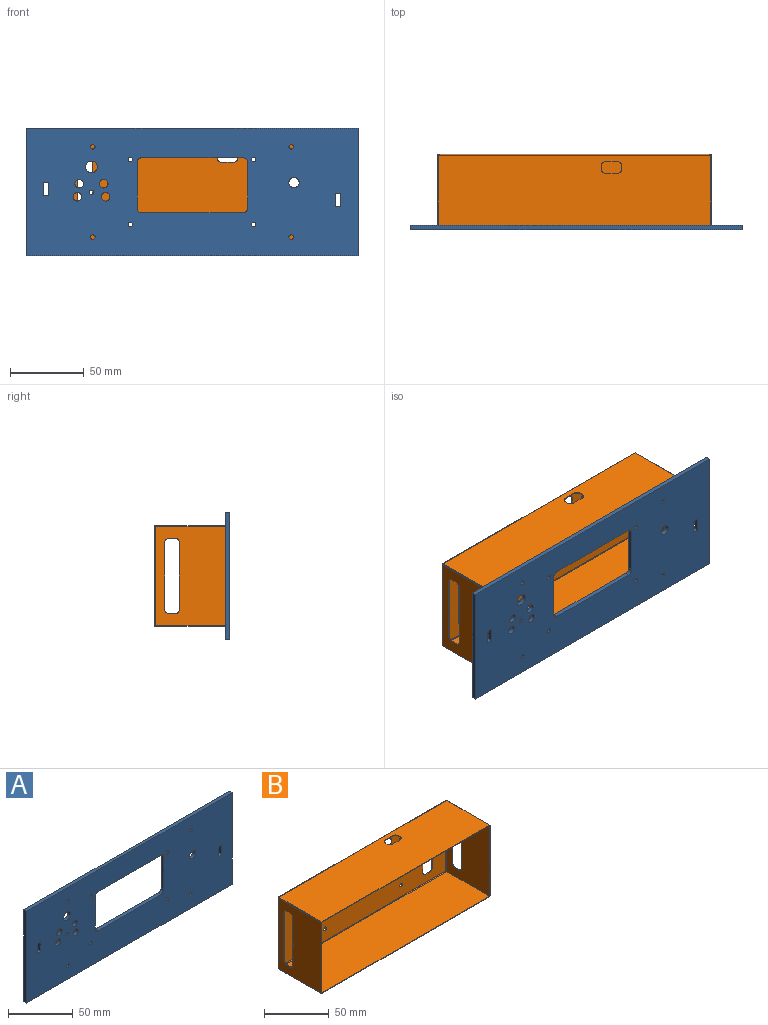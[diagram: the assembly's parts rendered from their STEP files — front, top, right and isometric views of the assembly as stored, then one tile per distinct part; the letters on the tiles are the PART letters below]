
ASSEMBLY  parts=2 mates=3
PART A: 37 faces, bbox 224.5x3x86.5 mm
  f0: plane 224.5x3mm, normal (0,0,1), area 673.5mm2, adj f1,f34,f35,f36
  f1: plane 86.5x3mm, normal (-1,0,0), area 259.5mm2, adj f0,f2,f35,f36
  f2: plane 224.5x3mm, normal (0,0,-1), area 673.5mm2, adj f1,f34,f35,f36
  f3: plane 9x3mm, normal (-1,0,0), area 27mm2, adj f4,f16,f35,f36
  f4: plane 4x3mm, normal (0,0,1), area 12mm2, adj f3,f5,f35,f36
  f5: plane 9x3mm, normal (1,0,0), area 27mm2, adj f4,f16,f35,f36
  f6: plane 9x3mm, normal (-1,0,0), area 27mm2, adj f7,f17,f35,f36
  f7: plane 4x3mm, normal (0,0,1), area 12mm2, adj f6,f8,f35,f36
  f8: plane 9x3mm, normal (1,0,0), area 27mm2, adj f7,f17,f35,f36
  f9: cylinder r=3mm len=3mm, axis (0,1,0), area 14.1mm2, adj f10,f18,f35,f36
  f10: plane 31x3mm, normal (-1,0,0), area 93mm2, adj f9,f11,f35,f36
  f11: cylinder r=3mm len=3mm, axis (0,1,0), area 14.1mm2, adj f10,f12,f35,f36
  f12: plane 68.81x3mm, normal (0,0,1), area 206.4mm2, adj f11,f13,f35,f36
  f13: cylinder r=3mm len=3mm, axis (0,1,0), area 14.1mm2, adj f12,f14,f35,f36
  f14: plane 31x3mm, normal (1,0,0), area 93mm2, adj f13,f15,f35,f36
  f15: cylinder r=3mm len=3mm, axis (0,1,0), area 14.1mm2, adj f14,f18,f35,f36
  f16: plane 4x3mm, normal (0,0,-1), area 12mm2, adj f3,f5,f35,f36
  f17: plane 4x3mm, normal (0,0,-1), area 12mm2, adj f6,f8,f35,f36
  f18: plane 68.81x3mm, normal (0,0,-1), area 206.4mm2, adj f9,f15,f35,f36
  f19: cylinder r=1.5mm len=3mm, axis (0,1,0), area 28.3mm2, adj f35,f36
  f20: cylinder r=1.5mm len=3mm, axis (0,1,0), area 28.3mm2, adj f35,f36
  f21: cylinder r=1.5mm len=3mm, axis (0,1,0), area 28.3mm2, adj f35,f36
  f22: cylinder r=1.5mm len=3mm, axis (0,1,0), area 28.3mm2, adj f35,f36
  f23: cylinder r=1.5mm len=3mm, axis (0,1,0), area 28.3mm2, adj f35,f36
  f24: cylinder r=1.5mm len=3mm, axis (0,1,0), area 28.3mm2, adj f35,f36
  f25: cylinder r=1.5mm len=3mm, axis (0,1,0), area 28.3mm2, adj f35,f36
  f26: cylinder r=1.5mm len=3mm, axis (0,1,0), area 28.3mm2, adj f35,f36
  f27: cylinder r=1.5mm len=3mm, axis (0,1,0), area 28.3mm2, adj f35,f36
  f28: cylinder r=4mm len=8mm, axis (0,1,0), area 75.4mm2, adj f35,f36
  f29: cylinder r=2.9mm len=5.8mm, axis (0,1,0), area 54.7mm2, adj f35,f36
  f30: cylinder r=2.9mm len=5.8mm, axis (0,1,0), area 54.7mm2, adj f35,f36
  f31: cylinder r=2.9mm len=5.8mm, axis (0,1,0), area 54.7mm2, adj f35,f36
  f32: cylinder r=2.9mm len=5.8mm, axis (0,1,0), area 54.7mm2, adj f35,f36
  f33: cylinder r=3.5mm len=7mm, axis (0,1,0), area 66mm2, adj f35,f36
  f34: plane 86.5x3mm, normal (1,0,0), area 259.5mm2, adj f0,f2,f35,f36
  f35: plane 224.5x86.5mm, normal (0,-1,0), area 16329mm2, adj f0,f1,f2,f3,f4,f5,f6,f7
  f36: plane 224.5x86.5mm, normal (0,1,0), area 16329mm2, adj f0,f1,f2,f3,f4,f5,f6,f7
PART B: 98 faces, bbox 185x48x68 mm
  f0: cylinder r=3mm len=3mm, axis (0,-1,0), area 2.4mm2, adj f1,f27,f28,f29
  f1: plane 45x0.5mm, normal (1,0,0), area 22.5mm2, adj f0,f2,f28,f29
  f2: cylinder r=3mm len=3mm, axis (0,-1,0), area 2.4mm2, adj f1,f3,f28,f29
  f3: plane 4x0.5mm, normal (0,0,1), area 2mm2, adj f2,f4,f28,f29
  f4: cylinder r=3mm len=3mm, axis (0,-1,0), area 2.4mm2, adj f3,f5,f28,f29
  f5: plane 45x0.5mm, normal (-1,0,0), area 22.5mm2, adj f4,f6,f28,f29
  f6: cylinder r=3mm len=3mm, axis (0,-1,0), area 2.4mm2, adj f5,f27,f28,f29
  f7: cylinder r=3mm len=3mm, axis (0,-1,0), area 2.4mm2, adj f8,f26,f28,f29
  f8: plane 3x0.5mm, normal (-1,0,0), area 1.5mm2, adj f7,f9,f28,f29
  f9: cylinder r=3mm len=3mm, axis (0,-1,0), area 2.4mm2, adj f8,f10,f28,f29
  f10: plane 8x0.5mm, normal (0,0,-1), area 4mm2, adj f9,f11,f28,f29
  f11: cylinder r=3mm len=3mm, axis (0,-1,0), area 2.4mm2, adj f10,f12,f28,f29
  f12: plane 3x0.5mm, normal (1,0,0), area 1.5mm2, adj f11,f13,f28,f29
  f13: cylinder r=3mm len=3mm, axis (0,-1,0), area 2.4mm2, adj f12,f26,f28,f29
  f14: plane 45x0.5mm, normal (1,0,0), area 22.5mm2, adj f15,f21,f28,f29
  f15: cylinder r=3mm len=3mm, axis (0,-1,0), area 2.4mm2, adj f14,f16,f28,f29
  f16: plane 4x0.5mm, normal (0,0,1), area 2mm2, adj f15,f17,f28,f29
  f17: cylinder r=3mm len=3mm, axis (0,-1,0), area 2.4mm2, adj f16,f18,f28,f29
  f18: plane 45x0.5mm, normal (-1,0,0), area 22.5mm2, adj f17,f19,f28,f29
  f19: cylinder r=3mm len=3mm, axis (0,-1,0), area 2.4mm2, adj f18,f20,f28,f29
  f20: plane 4x0.5mm, normal (0,0,-1), area 2mm2, adj f19,f21,f28,f29
  f21: cylinder r=3mm len=3mm, axis (0,-1,0), area 2.4mm2, adj f14,f20,f28,f29
  f22: cylinder r=1.5mm len=3mm, axis (0,-1,0), area 4.7mm2, adj f28,f29
  f23: cylinder r=1.5mm len=3mm, axis (0,-1,0), area 4.7mm2, adj f28,f29
  f24: cylinder r=1.5mm len=3mm, axis (0,-1,0), area 4.7mm2, adj f28,f29
  f25: cylinder r=1.5mm len=3mm, axis (0,-1,0), area 4.7mm2, adj f28,f29
  f26: plane 8x0.5mm, normal (0,0,1), area 4mm2, adj f7,f13,f28,f29
  f27: plane 4x0.5mm, normal (0,0,-1), area 2mm2, adj f0,f6,f28,f29
  f28: plane 183x66mm, normal (0,1,0), area 10926.9mm2, adj f0,f1,f2,f3,f4,f5,f6,f7
  f29: plane 183x66mm, normal (0,-1,0), area 10926.9mm2, adj f0,f1,f2,f3,f4,f5,f6,f7
  f30: plane 0.5x0.48mm, normal (0,1,0), area 0.2mm2, adj f32,f35,f36,f38
  f31: plane 183.96x0.5mm, normal (0,-1,0), area 92mm2, adj f32,f34,f35,f36
  f32: plane 47x0.5mm, normal (-1,0,0), area 23.5mm2, adj f30,f31,f35,f36
  f33: plane 0.5x0.48mm, normal (0,1,0), area 0.2mm2, adj f34,f35,f36,f37
  f34: plane 47x0.5mm, normal (1,0,0), area 23.5mm2, adj f31,f33,f35,f36
  f35: plane 183.96x47mm, normal (0,0,-1), area 8646.1mm2, adj f30,f31,f32,f33,f34,f39
  f36: plane 183.96x47mm, normal (0,0,1), area 8646.1mm2, adj f30,f31,f32,f33,f34,f40
  f37: plane 1x1mm, normal (1,0,0), area 0.6mm2, adj f33,f39,f40,f76
  f38: plane 1x1mm, normal (-1,0,0), area 0.6mm2, adj f30,f39,f40,f94
  f39: cylinder r=1mm len=183mm, axis (1,0,0), area 287.5mm2, adj f28,f35,f37,f38
  f40: cylinder r=0.5mm len=183mm, axis (1,0,0), area 143.7mm2, adj f29,f36,f37,f38
  f41: plane 0.5x0.48mm, normal (0,1,0), area 0.2mm2, adj f50,f54,f55,f57
  f42: plane 2x0.5mm, normal (-1,0,0), area 1mm2, adj f43,f53,f54,f55
  f43: cylinder r=3mm len=3mm, axis (0,0,1), area 2.4mm2, adj f42,f44,f54,f55
  f44: plane 8x0.5mm, normal (0,1,0), area 4mm2, adj f43,f45,f54,f55
  f45: cylinder r=3mm len=3mm, axis (0,0,1), area 2.4mm2, adj f44,f46,f54,f55
  f46: plane 2x0.5mm, normal (1,0,0), area 1mm2, adj f45,f47,f54,f55
  f47: cylinder r=3mm len=3mm, axis (0,0,1), area 2.4mm2, adj f46,f48,f54,f55
  f48: plane 8x0.5mm, normal (0,-1,0), area 4mm2, adj f47,f53,f54,f55
  f49: plane 183.96x0.5mm, normal (0,-1,0), area 92mm2, adj f50,f52,f54,f55
  f50: plane 47x0.5mm, normal (1,0,0), area 23.5mm2, adj f41,f49,f54,f55
  f51: plane 0.5x0.48mm, normal (0,1,0), area 0.2mm2, adj f52,f54,f55,f56
  f52: plane 47x0.5mm, normal (-1,0,0), area 23.5mm2, adj f49,f51,f54,f55
  f53: cylinder r=3mm len=3mm, axis (0,0,1), area 2.4mm2, adj f42,f48,f54,f55
  f54: plane 183.96x47mm, normal (0,0,1), area 8541.8mm2, adj f41,f42,f43,f44,f45,f46,f47,f48
  f55: plane 183.96x47mm, normal (0,0,-1), area 8541.8mm2, adj f41,f42,f43,f44,f45,f46,f47,f48
  f56: plane 1x1mm, normal (-1,0,0), area 0.6mm2, adj f51,f58,f59,f95
  f57: plane 1x1mm, normal (1,0,0), area 0.6mm2, adj f41,f58,f59,f75
  f58: cylinder r=1mm len=183mm, axis (-1,0,0), area 287.5mm2, adj f28,f54,f56,f57
  f59: cylinder r=0.5mm len=183mm, axis (-1,0,0), area 143.7mm2, adj f29,f55,f56,f57
  f60: plane 0.5x0.48mm, normal (0,1,0), area 0.2mm2, adj f62,f73,f74,f76
  f61: plane 66.96x0.5mm, normal (0,-1,0), area 33.5mm2, adj f62,f72,f73,f74
  f62: plane 47x0.5mm, normal (0,0,-1), area 23.5mm2, adj f60,f61,f73,f74
  f63: plane 0.5x0.48mm, normal (0,1,0), area 0.2mm2, adj f72,f73,f74,f75
  f64: cylinder r=3mm len=3mm, axis (1,0,0), area 2.4mm2, adj f65,f71,f73,f74
  f65: plane 4x0.5mm, normal (0,0,-1), area 2mm2, adj f64,f66,f73,f74
  f66: cylinder r=3mm len=3mm, axis (1,0,0), area 2.4mm2, adj f65,f67,f73,f74
  f67: plane 45x0.5mm, normal (0,-1,0), area 22.5mm2, adj f66,f68,f73,f74
  f68: cylinder r=3mm len=3mm, axis (1,0,0), area 2.4mm2, adj f67,f69,f73,f74
  f69: plane 4x0.5mm, normal (0,0,1), area 2mm2, adj f68,f70,f73,f74
  f70: cylinder r=3mm len=3mm, axis (1,0,0), area 2.4mm2, adj f69,f71,f73,f74
  f71: plane 45x0.5mm, normal (0,1,0), area 22.5mm2, adj f64,f70,f73,f74
  f72: plane 47x0.5mm, normal (0,0,1), area 23.5mm2, adj f61,f63,f73,f74
  f73: plane 66.96x47mm, normal (1,0,0), area 2644.8mm2, adj f60,f61,f62,f63,f64,f65,f66,f67
  f74: plane 66.96x47mm, normal (-1,0,0), area 2644.8mm2, adj f60,f61,f62,f63,f64,f65,f66,f67
  f75: plane 1x1mm, normal (0,0,1), area 0.6mm2, adj f57,f63,f77,f78
  f76: plane 1x1mm, normal (0,0,-1), area 0.6mm2, adj f37,f60,f77,f78
  f77: cylinder r=1mm len=66mm, axis (0,0,1), area 103.7mm2, adj f28,f73,f75,f76
  f78: cylinder r=0.5mm len=66mm, axis (0,0,1), area 51.8mm2, adj f29,f74,f75,f76
  f79: plane 0.5x0.48mm, normal (0,1,0), area 0.2mm2, adj f81,f92,f93,f95
  f80: plane 66.96x0.5mm, normal (0,-1,0), area 33.5mm2, adj f81,f91,f92,f93
  f81: plane 47x0.5mm, normal (0,0,1), area 23.5mm2, adj f79,f80,f92,f93
  f82: plane 0.5x0.48mm, normal (0,1,0), area 0.2mm2, adj f91,f92,f93,f94
  f83: cylinder r=3mm len=3mm, axis (-1,0,0), area 2.4mm2, adj f84,f90,f92,f93
  f84: plane 4x0.5mm, normal (0,0,1), area 2mm2, adj f83,f85,f92,f93
  f85: cylinder r=3mm len=3mm, axis (-1,0,0), area 2.4mm2, adj f84,f86,f92,f93
  f86: plane 45x0.5mm, normal (0,-1,0), area 22.5mm2, adj f85,f87,f92,f93
  f87: cylinder r=3mm len=3mm, axis (-1,0,0), area 2.4mm2, adj f86,f88,f92,f93
  f88: plane 4x0.5mm, normal (0,0,-1), area 2mm2, adj f87,f89,f92,f93
  f89: cylinder r=3mm len=3mm, axis (-1,0,0), area 2.4mm2, adj f88,f90,f92,f93
  f90: plane 45x0.5mm, normal (0,1,0), area 22.5mm2, adj f83,f89,f92,f93
  f91: plane 47x0.5mm, normal (0,0,-1), area 23.5mm2, adj f80,f82,f92,f93
  f92: plane 66.96x47mm, normal (-1,0,0), area 2644.8mm2, adj f79,f80,f81,f82,f83,f84,f85,f86
  f93: plane 66.96x47mm, normal (1,0,0), area 2644.8mm2, adj f79,f80,f81,f82,f83,f84,f85,f86
  f94: plane 1x1mm, normal (0,0,-1), area 0.6mm2, adj f38,f82,f96,f97
  f95: plane 1x1mm, normal (0,0,1), area 0.6mm2, adj f56,f79,f96,f97
  f96: cylinder r=1mm len=66mm, axis (0,0,-1), area 103.7mm2, adj f28,f92,f94,f95
  f97: cylinder r=0.5mm len=66mm, axis (0,0,-1), area 51.8mm2, adj f29,f93,f94,f95
PLACE A t=(2,0,0)mm
PLACE B t=(182,1,0)mm fixed
MATE cylindrical A.f26 <-> B.f25  axis (0,1,0) through (132.16,-48.5,55.97)mm
MATE planar B.f49 <-> A.f36  axis (0,-1,0) through (89.5,-47,67.75)mm
MATE cylindrical A.f24 <-> B.f24  axis (0,1,0) through (48.84,-50,12.03)mm
